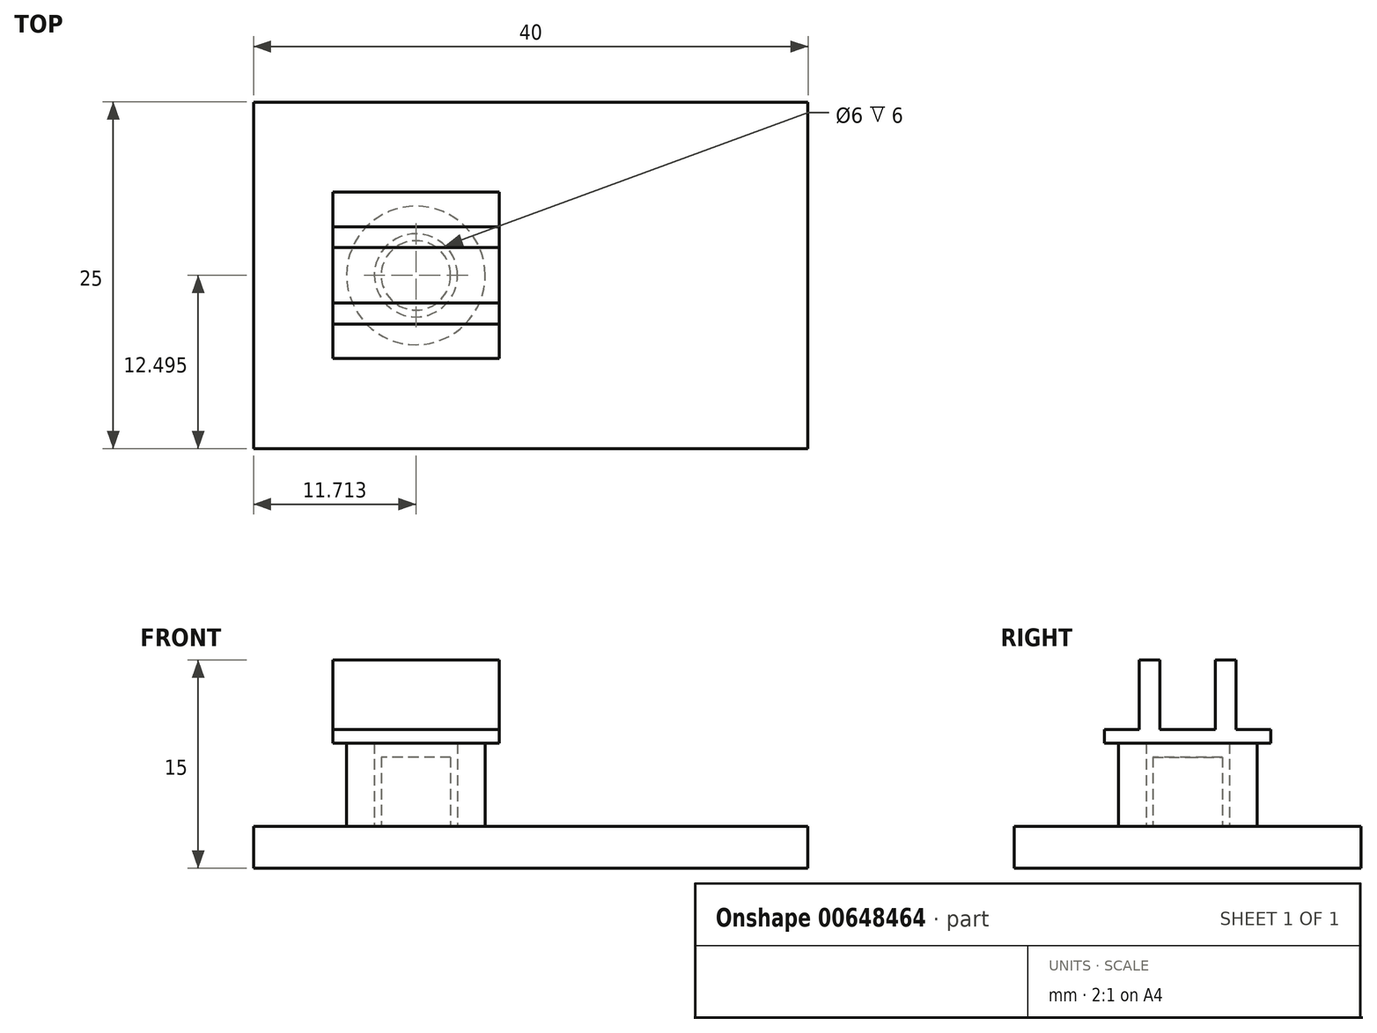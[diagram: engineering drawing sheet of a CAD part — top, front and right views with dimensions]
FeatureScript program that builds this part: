
annotation { "Feature Type Name" : "Feature", "Feature Type Description" : "" }
export const myFeature = defineFeature(function(context is Context, id is Id, definition is map)
    precondition{}
    {
        {
            var Q0;
            Q0=qCreatedBy(makeId("Top.planeOp"),FACE);
            var sketch = newSketch(context, id + "F0", { "sketchPlane" : qUnion([Q0])});
            skLineSegment(sketch, "E0.bottom", {"start": v(-48.6, 12.73) * mm, "end": v(-8.6, 12.73) * mm});
            skLineSegment(sketch, "E0.top", {"start": v(-48.6, -12.27) * mm, "end": v(-8.6, -12.27) * mm});
            skLineSegment(sketch, "E0.left", {"start": v(-48.6, 12.73) * mm, "end": v(-48.6, -12.27) * mm});
            skLineSegment(sketch, "E0.right", {"start": v(-8.6, 12.73) * mm, "end": v(-8.6, -12.27) * mm});
            skSolve(sketch);
        }
        {
            var Q0;
            Q0=makeQuery(id+"F0.imprint","IMPRINT",FACE,{"disambiguationData":[TD([[makeQuery(id+"F0.imprint","IMPRINT",EDGE,{"derivedFrom":sQuery(id+"F0.wireOp",EDGE,"E0.bottom")}),-1.0]])]});
            extrude(context, id + "F1", {"entities" : qUnion([Q0]), "depth" : 3 * mm, "offsetDistance" : 25 * mm});
        }
        {
            var Q0;
            Q0=makeQuery(id+"F1.opExtrude","CAP_FACE",FACE,{"disambiguationData":[OSD([sQuery(id+"F0.wireOp",EDGE,"E0.bottom"),sQuery(id+"F0.wireOp",EDGE,"E0.top"),sQuery(id+"F0.wireOp",EDGE,"E0.left"),sQuery(id+"F0.wireOp",EDGE,"E0.right")])],"isStart":false});
            var sketch = newSketch(context, id + "F2", { "sketchPlane" : qUnion([Q0])});
            skCircle(sketch, "E1", {"center": v(-36.89, 0.23) * mm, "radius": 2.5 * mm});
            skSolve(sketch);
        }
        {
            var Q0;
            Q0=makeQuery(id+"F2.imprint","IMPRINT",FACE,{"disambiguationData":[TD([[makeQuery(id+"F2.imprint","IMPRINT",EDGE,{"derivedFrom":sQuery(id+"F2.wireOp",EDGE,"E1")}),1.0]])]});
            extrude(context, id + "F3", {"entities" : qUnion([Q0]), "operationType" : NewBodyOperationType.ADD, "depth" : 5 * mm, "offsetDistance" : 25 * mm});
        }
        {
            var Q0;
            Q0=makeQuery(id+"F1.opExtrude","CAP_FACE",FACE,{"disambiguationData":[OSD([sQuery(id+"F0.wireOp",EDGE,"E0.bottom"),sQuery(id+"F0.wireOp",EDGE,"E0.top"),sQuery(id+"F0.wireOp",EDGE,"E0.left"),sQuery(id+"F0.wireOp",EDGE,"E0.right")])],"isStart":false});
            var sketch = newSketch(context, id + "F4", { "sketchPlane" : qUnion([Q0])});
            skCircle(sketch, "E2", {"center": v(-36.89, 0.23) * mm, "radius": 5 * mm});
            skCircle(sketch, "E3", {"center": v(-36.89, 0.23) * mm, "radius": 3 * mm});
            skSolve(sketch);
        }
        {
            var Q0;
            Q0=makeQuery(id+"F4.imprint","IMPRINT",FACE,{"disambiguationData":[TD([[makeQuery(id+"F4.imprint","IMPRINT",EDGE,{"derivedFrom":sQuery(id+"F4.wireOp",EDGE,"E2")}),1.0]])]});
            extrude(context, id + "F5", {"entities" : qUnion([Q0]), "depth" : 6 * mm, "offsetDistance" : 25 * mm});
        }
        {
            var Q0;
            Q0=makeQuery(id+"F5.opExtrude","CAP_FACE",FACE,{"disambiguationData":[OSD([sQuery(id+"F4.wireOp",EDGE,"E2"),sQuery(id+"F4.wireOp",EDGE,"E3")])],"isStart":false});
            var sketch = newSketch(context, id + "F6", { "sketchPlane" : qUnion([Q0])});
            skLineSegment(sketch, "E4.bottom", {"start": v(-42.89, 6.23) * mm, "end": v(-30.89, 6.23) * mm});
            skLineSegment(sketch, "E4.top", {"start": v(-42.89, -5.77) * mm, "end": v(-30.89, -5.77) * mm});
            skLineSegment(sketch, "E4.left", {"start": v(-42.89, 6.23) * mm, "end": v(-42.89, -5.77) * mm});
            skLineSegment(sketch, "E4.right", {"start": v(-30.89, 6.23) * mm, "end": v(-30.89, -5.77) * mm});
            skSolve(sketch);
        }
        {
            var Q0;
            Q0=makeQuery(id+"F6.imprint","IMPRINT",FACE,{"disambiguationData":[TD([[makeQuery(id+"F6.imprint","IMPRINT",EDGE,{"derivedFrom":sQuery(id+"F6.wireOp",EDGE,"E4.bottom")}),-1.0]])]});
            var Q1;
            Q1=makeQuery(id+"F6.imprint","IMPRINT",FACE,{"disambiguationData":[TD([[makeQuery(id+"F6.imprint","IMPRINT",EDGE,{"derivedFrom":makeQuery(id+"F5.opExtrude","CAP_EDGE",EDGE,{"disambiguationData":[OSD([sQuery(id+"F4.wireOp",EDGE,"E2")])],"isStart":false})}),1.0]])]});
            var Q2;
            Q2=makeQuery(id+"F6.imprint","IMPRINT",FACE,{"disambiguationData":[TD([[makeQuery(id+"F6.imprint","IMPRINT",EDGE,{"derivedFrom":makeQuery(id+"F5.opExtrude","CAP_EDGE",EDGE,{"disambiguationData":[OSD([sQuery(id+"F4.wireOp",EDGE,"E3")])],"isStart":false})}),1.0]])]});
            extrude(context, id + "F7", {"entities" : qUnion([Q0, Q1, Q2]), "operationType" : NewBodyOperationType.ADD, "depth" : 1 * mm, "offsetDistance" : 25 * mm});
        }
        {
            var Q0;
            Q0=makeQuery(id+"F7.opExtrude","CAP_FACE",FACE,{"disambiguationData":[OSD([sQuery(id+"F6.wireOp",EDGE,"E4.bottom"),sQuery(id+"F6.wireOp",EDGE,"E4.top"),sQuery(id+"F6.wireOp",EDGE,"E4.left"),sQuery(id+"F6.wireOp",EDGE,"E4.right")])],"isStart":false});
            var sketch = newSketch(context, id + "F8", { "sketchPlane" : qUnion([Q0])});
            skLineSegment(sketch, "E5.bottom", {"start": v(-42.89, 3.73) * mm, "end": v(-30.89, 3.73) * mm});
            skLineSegment(sketch, "E5.top", {"start": v(-42.89, 2.23) * mm, "end": v(-30.89, 2.23) * mm});
            skLineSegment(sketch, "E5.left", {"start": v(-42.89, 3.73) * mm, "end": v(-42.89, 2.23) * mm});
            skLineSegment(sketch, "E5.right", {"start": v(-30.89, 3.73) * mm, "end": v(-30.89, 2.23) * mm});
            skLineSegment(sketch, "E6.bottom", {"start": v(-42.89, -1.77) * mm, "end": v(-30.89, -1.77) * mm});
            skLineSegment(sketch, "E6.top", {"start": v(-42.89, -3.27) * mm, "end": v(-30.89, -3.27) * mm});
            skLineSegment(sketch, "E6.left", {"start": v(-42.89, -1.77) * mm, "end": v(-42.89, -3.27) * mm});
            skLineSegment(sketch, "E6.right", {"start": v(-30.89, -1.77) * mm, "end": v(-30.89, -3.27) * mm});
            skSolve(sketch);
        }
        {
            var Q0;
            Q0=makeQuery(id+"F8.imprint","IMPRINT",FACE,{"disambiguationData":[TD([[makeQuery(id+"F8.imprint","IMPRINT",EDGE,{"derivedFrom":sQuery(id+"F8.wireOp",EDGE,"E5.bottom")}),-1.0]])]});
            var Q1;
            Q1=makeQuery(id+"F8.imprint","IMPRINT",FACE,{"disambiguationData":[TD([[makeQuery(id+"F8.imprint","IMPRINT",EDGE,{"derivedFrom":sQuery(id+"F8.wireOp",EDGE,"E6.bottom")}),-1.0]])]});
            extrude(context, id + "F9", {"entities" : qUnion([Q0, Q1]), "operationType" : NewBodyOperationType.ADD, "depth" : 5 * mm, "offsetDistance" : 25 * mm});
        }
    });
